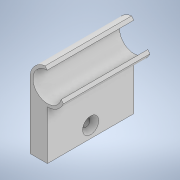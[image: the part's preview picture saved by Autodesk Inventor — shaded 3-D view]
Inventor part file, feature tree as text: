
AUTODESK INVENTOR PART (.ipt)
format: ipt  version: 2021.2 (Build 252289000, 289)  size: 198,144 bytes
history: native  units: in
note: dims shown in document units (in); Inventor stores cm internally (conversion verified against a paired STEP export)
features: sketch x4, extrude x3, hole x1
ambient origin geometry x8: Origin, YZ Plane, XZ Plane, XY Plane, X Axis, Y Axis, Z Axis, Center Point
bodies: Body1 (feature_tree)
feature tree (8):
  extrude  "Extrusion3"  Depth=0.05in
  extrude  "Extrusion4"  Depth=0.4in
  hole  "Hole1"  [1 undecoded]
  extrude  "Text"  Depth=0.2in
  sketch  "Sketch4"  dims[d10=0.5in d11=0.05in]
  sketch  "Sketch5"  dims[d12=0.2577in d13=0.4in]
  sketch  "Sketch6"  dims[d14=1.5in d15=0.0in]
  sketch  "Sketch10"  dims[d16=0.85in d17=1.5in d18=0.0in d19=0.138in d20=0.75in d21=0.28in d22=0.25in d23=0.5635in d24=0.29in d25=0.0in d28=0.045in d29=0.0in d30=0.2in d31=0.0in]
note: 1 required parameter value undecoded (feature->parameter linkage not recoverable at this tier; creation-order binding heuristic only, values carry confidence <= 0.55)
